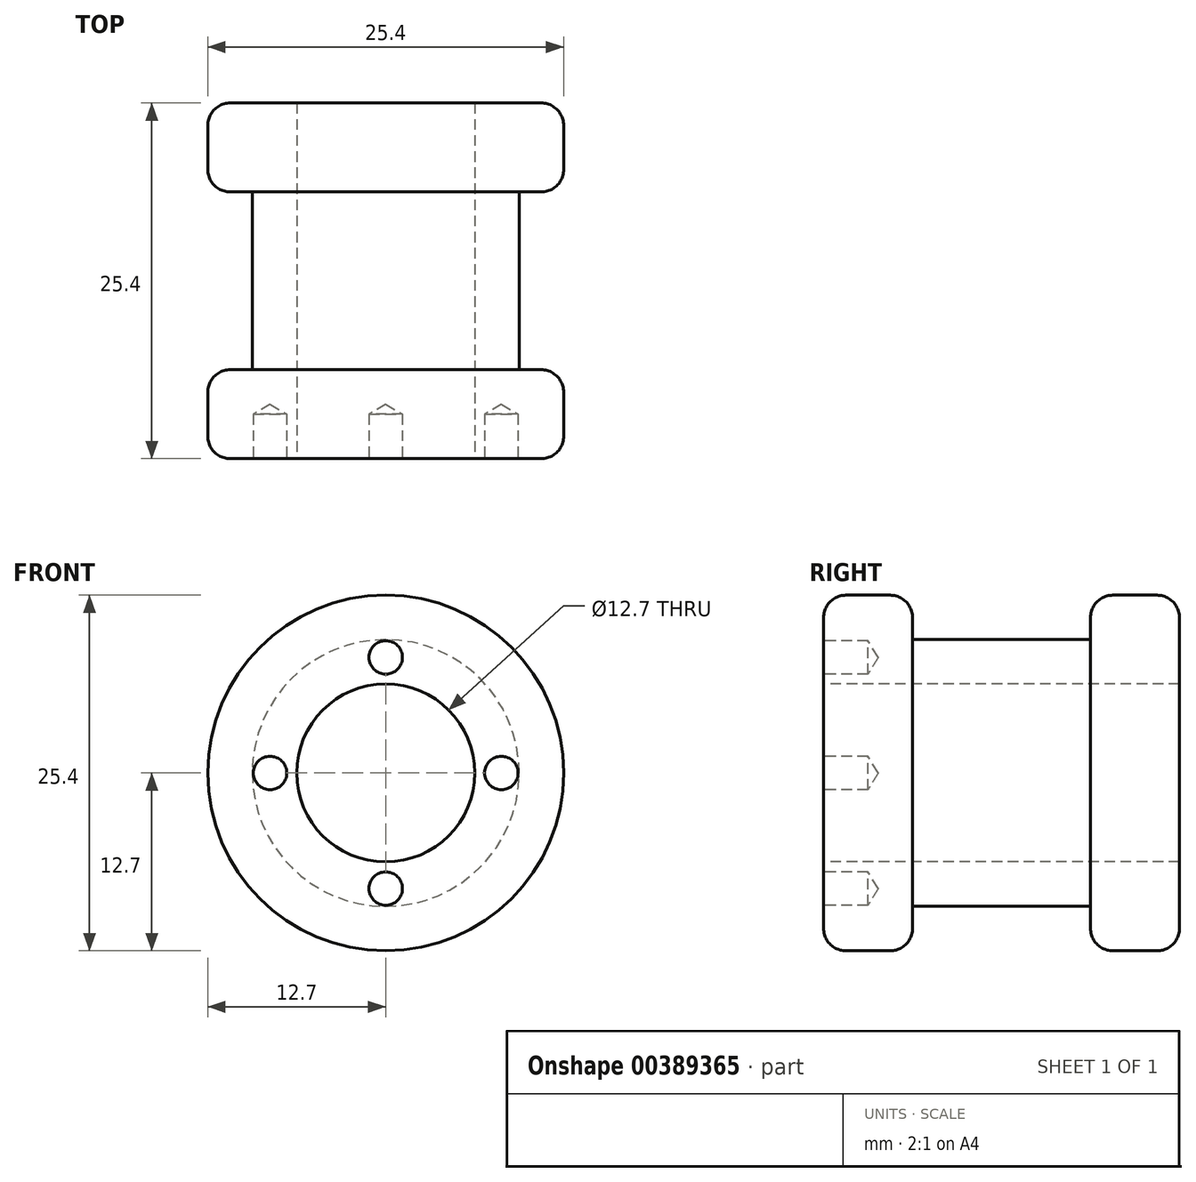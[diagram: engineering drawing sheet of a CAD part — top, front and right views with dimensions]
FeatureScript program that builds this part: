
annotation { "Feature Type Name" : "Feature", "Feature Type Description" : "" }
export const myFeature = defineFeature(function(context is Context, id is Id, definition is map)
    precondition{}
    {
        {
            var Q0;
            Q0=qCreatedBy(makeId("Front.planeOp"),FACE);
            var sketch = newSketch(context, id + "F0", { "sketchPlane" : qUnion([Q0])});
            skCircle(sketch, "E0", {"center": v(0, 0) * mm, "radius": 12.7 * mm});
            skSolve(sketch);
        }
        {
            var Q0;
            Q0 = qSketchRegion(id + "F0", true);
            extrude(context, id + "F1", {"entities" : qUnion([Q0]), "depth" : 6.35 * mm});
        }
        {
            var Q0;
            Q0=makeQuery(id+"F1.opExtrude","CAP_FACE",FACE,{"disambiguationData":[OSD([sQuery(id+"F0.wireOp",EDGE,"E0")])],"isStart":true});
            var sketch = newSketch(context, id + "F2", { "sketchPlane" : qUnion([Q0])});
            skCircle(sketch, "E1", {"center": v(0, 0) * mm, "radius": 9.53 * mm});
            skSolve(sketch);
        }
        {
            var Q0;
            Q0 = qSketchRegion(id + "F2", true);
            extrude(context, id + "F3", {"entities" : qUnion([Q0]), "operationType" : NewBodyOperationType.ADD, "depth" : 12.7 * mm});
        }
        {
            var Q0;
            Q0=makeQuery(id+"F3.opExtrude","CAP_FACE",FACE,{"disambiguationData":[OSD([sQuery(id+"F2.wireOp",EDGE,"E1")])],"isStart":false});
            var sketch = newSketch(context, id + "F4", { "sketchPlane" : qUnion([Q0])});
            skCircle(sketch, "E2", {"center": v(0, 0) * mm, "radius": 12.7 * mm});
            skSolve(sketch);
        }
        {
            var Q0;
            Q0 = qSketchRegion(id + "F4", true);
            extrude(context, id + "F5", {"entities" : qUnion([Q0]), "operationType" : NewBodyOperationType.ADD, "depth" : 6.35 * mm});
        }
        {
            var Q0;
            Q0=makeQuery(id+"F1.opExtrude","CAP_FACE",FACE,{"disambiguationData":[OSD([sQuery(id+"F0.wireOp",EDGE,"E0")])],"isStart":false});
            var sketch = newSketch(context, id + "F6", { "sketchPlane" : qUnion([Q0])});
            skCircle(sketch, "E3", {"center": v(0, 0) * mm, "radius": 9.53 * mm, "construction": true});
            skCircle(sketch, "E4", {"center": v(0, -8.26) * mm, "radius": 1.2 * mm});
            skCircle(sketch, "E5", {"center": v(0, 0) * mm, "radius": 6.35 * mm});
            skLineSegment(sketch, "E6", {"start": v(-12.7, 0) * mm, "end": v(12.7, 0) * mm, "construction": true});
            skCircle(sketch, "E7.MirrorC", {"center": v(0, 8.26) * mm, "radius": 1.2 * mm});
            skCircle(sketch, "E8", {"center": v(-8.26, 0) * mm, "radius": 1.2 * mm});
            skLineSegment(sketch, "E9", {"start": v(0, 12.7) * mm, "end": v(0, -12.7) * mm, "construction": true});
            skCircle(sketch, "E10.MirrorC", {"center": v(8.26, 0) * mm, "radius": 1.2 * mm});
            skSolve(sketch);
        }
        {
            var Q0;
            Q0=sQuery(id+"F6.wireOp",VERTEX,"E8.center");
            var Q1;
            Q1=sQuery(id+"F6.wireOp",VERTEX,"E4.center");
            var Q2;
            Q2=sQuery(id+"F6.wireOp",VERTEX,"E10.MirrorC.center");
            var Q3;
            Q3=sQuery(id+"F6.wireOp",VERTEX,"E7.MirrorC.center");
            var Q4;
            Q4=makeQuery(id+"F1.opExtrude","SWEPT_BODY",BODY,{"disambiguationData":[OSD([sQuery(id+"F0.wireOp",EDGE,"E0")])]});
            hole(context, id + "F7", {"style" : HoleStyle.SIMPLE, "endStyle" : HoleEndStyle.BLIND, "holeDiameter" : 2.4 * mm, "holeDepth" : 3.17 * mm, "isTappedThrough" : true, "tappedDepth" : 12.7 * mm, "tapClearance" : 3, "locations" : qUnion([Q0, Q1, Q2, Q3]), "scope" : qUnion([Q4])});
        }
        {
            var Q0;
            Q0=makeQuery(id+"F1.opExtrude","CAP_EDGE",EDGE,{"disambiguationData":[OSD([sQuery(id+"F0.wireOp",EDGE,"E0")])],"isStart":false});
            var Q1;
            Q1=makeQuery(id+"F1.opExtrude","CAP_EDGE",EDGE,{"disambiguationData":[OSD([sQuery(id+"F0.wireOp",EDGE,"E0")])],"isStart":true});
            var Q2;
            Q2=makeQuery(id+"F5.opExtrude","CAP_EDGE",EDGE,{"disambiguationData":[OSD([sQuery(id+"F4.wireOp",EDGE,"E2")])],"isStart":false});
            var Q3;
            Q3=makeQuery(id+"F5.opExtrude","CAP_EDGE",EDGE,{"disambiguationData":[OSD([sQuery(id+"F4.wireOp",EDGE,"E2")])],"isStart":true});
            fillet(context, id + "F8", {"entities" : qUnion([Q0, Q1, Q2, Q3]), "radius" : 1.6 * mm, "tangentPropagation" : true, "allowEdgeOverflow" : false});
        }
        {
            var Q0;
            Q0=makeQuery(id+"F1.opExtrude","CAP_FACE",FACE,{"disambiguationData":[OSD([sQuery(id+"F0.wireOp",EDGE,"E0")])],"isStart":false});
            var sketch = newSketch(context, id + "F9", { "sketchPlane" : qUnion([Q0])});
            skCircle(sketch, "E11", {"center": v(0, 0) * mm, "radius": 6.35 * mm});
            skSolve(sketch);
        }
        {
            var Q0;
            Q0 = qSketchRegion(id + "F9", true);
            extrude(context, id + "F10", {"entities" : qUnion([Q0]), "operationType" : NewBodyOperationType.REMOVE, "endBound" : BoundingType.THROUGH_ALL, "oppositeDirection" : true, "depth" : 25.4 * mm});
        }
    });
